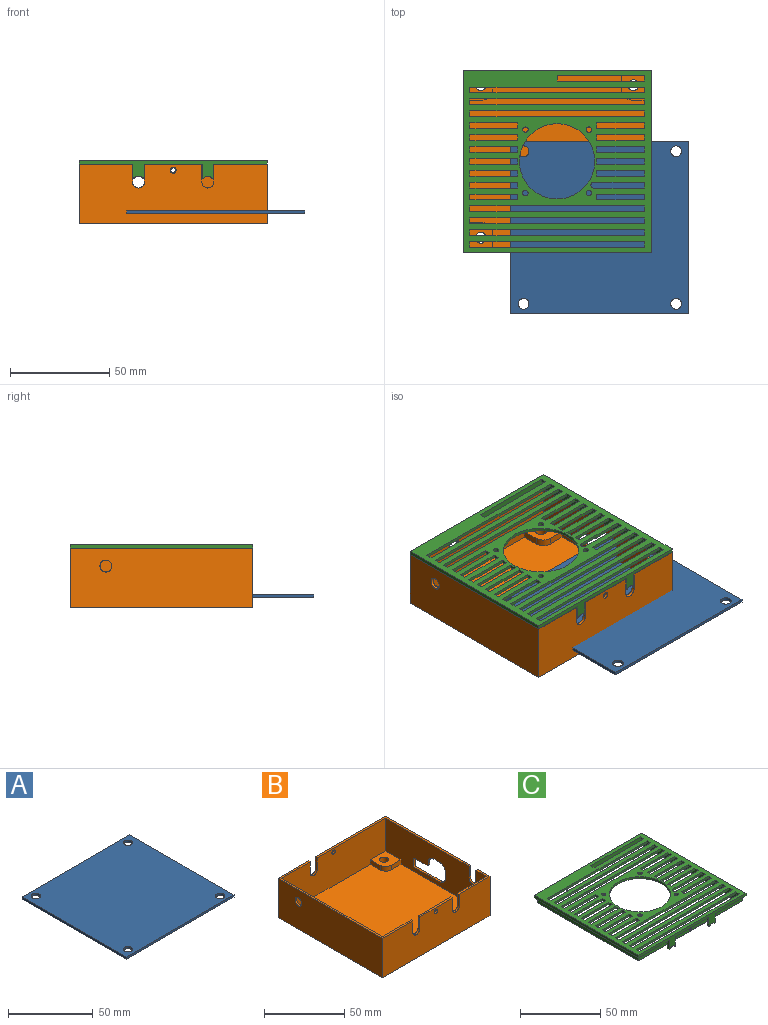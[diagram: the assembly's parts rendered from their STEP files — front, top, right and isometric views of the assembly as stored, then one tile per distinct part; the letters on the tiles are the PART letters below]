
ASSEMBLY  parts=3 mates=3
PART A: 10 faces, bbox 90x87x1.5 mm
  f0: plane 90x1.5mm, normal (0,1,0), area 135mm2, adj f1,f3,f4,f5
  f1: plane 87x1.5mm, normal (-1,0,0), area 130.5mm2, adj f0,f2,f4,f5
  f2: plane 90x1.5mm, normal (0,-1,0), area 135mm2, adj f1,f3,f4,f5
  f3: plane 87x1.5mm, normal (1,0,0), area 130.5mm2, adj f0,f2,f4,f5
  f4: plane 90x87mm, normal (0,0,1), area 7735mm2, adj f0,f1,f2,f3,f6,f7,f8,f9
  f5: plane 90x87mm, normal (0,0,-1), area 7735mm2, adj f0,f1,f2,f3,f6,f7,f8,f9
  f6: cylinder r=2.75mm len=5.5mm, axis (0,0,-1), area 25.9mm2, adj f4,f5
  f7: cylinder r=2.75mm len=5.5mm, axis (0,0,-1), area 25.9mm2, adj f4,f5
  f8: cylinder r=2.75mm len=5.5mm, axis (0,0,-1), area 25.9mm2, adj f4,f5
  f9: cylinder r=2.75mm len=5.5mm, axis (0,0,-1), area 25.9mm2, adj f4,f5
PART B: 61 faces, bbox 95x92x30 mm
  f0: plane 95x30mm, normal (0,-1,0), area 2706.7mm2, adj f2,f3,f5,f6,f12,f13,f49,f50
  f1: plane 75x62mm, normal (0,0,1), area 203.2mm2, adj f4,f5,f8,f11,f35,f52
  f2: plane 29x1.5mm, normal (0,0,1), area 43.5mm2, adj f0,f10,f49,f57
  f3: plane 27x11mm, normal (0,0,1), area 54.8mm2, adj f0,f4,f5,f10,f34,f51
  f4: plane 89x28.5mm, normal (-1,0,0), area 2074.2mm2, adj f1,f3,f7,f8,f10,f20,f22,f23
  f5: plane 92x30mm, normal (1,0,0), area 2392.2mm2, adj f0,f1,f3,f11,f13,f34,f35,f36
  f6: plane 92x27mm, normal (0,0,1), area 214.5mm2, adj f0,f8,f9,f10,f11,f12,f54,f55
  f7: plane 92x89mm, normal (0,0,1), area 7480.5mm2, adj f4,f8,f9,f10,f14,f15,f18,f19
  f8: plane 92x28.5mm, normal (0,-1,0), area 2452.3mm2, adj f1,f4,f6,f7,f9,f17,f19,f20
  f9: plane 89x28.5mm, normal (1,0,0), area 2413.7mm2, adj f6,f7,f8,f10,f15,f16,f17,f18
  f10: plane 92x28.5mm, normal (0,1,0), area 2384.2mm2, adj f2,f3,f4,f6,f7,f9,f14,f16
  f11: plane 95x30mm, normal (0,1,0), area 2774.8mm2, adj f1,f5,f6,f12,f13,f52,f53,f54
  f12: plane 92x30mm, normal (-1,0,0), area 2731.7mm2, adj f0,f6,f11,f13,f60
  f13: plane 95x92mm, normal (0,0,-1), area 8645mm2, adj f0,f5,f11,f12,f30,f31,f32,f33
  f14: plane 8.5x3.5mm, normal (1,0,0), area 29.8mm2, adj f7,f10,f16,f29
  f15: plane 8.5x3.5mm, normal (0,1,0), area 29.8mm2, adj f7,f9,f16,f29
  f16: plane 13.5x13.5mm, normal (0,0,1), area 153.1mm2, adj f9,f10,f14,f15,f29,f33
  f17: plane 13.5x13.5mm, normal (0,0,1), area 153.1mm2, adj f8,f9,f18,f19,f28,f32
  f18: plane 8.5x3.5mm, normal (0,-1,0), area 29.8mm2, adj f7,f9,f17,f28
  f19: plane 8.5x3.5mm, normal (1,0,0), area 29.8mm2, adj f7,f8,f17,f28
  f20: plane 13.5x13.5mm, normal (0,0,1), area 153.1mm2, adj f4,f8,f21,f22,f27,f31
  f21: plane 8.5x3.5mm, normal (-1,0,0), area 29.8mm2, adj f7,f8,f20,f27
  f22: plane 8.5x3.5mm, normal (0,-1,0), area 29.8mm2, adj f4,f7,f20,f27
  f23: plane 8.5x3.5mm, normal (0,1,0), area 29.8mm2, adj f4,f7,f25,f26
  f24: plane 8.5x3.5mm, normal (-1,0,0), area 29.8mm2, adj f7,f10,f25,f26
  f25: plane 13.5x13.5mm, normal (0,0,1), area 153.1mm2, adj f4,f10,f23,f24,f26,f30
  f26: cylinder r=5mm len=5mm, axis (0,0,1), area 27.5mm2, adj f7,f23,f24,f25
  f27: cylinder r=5mm len=5mm, axis (0,0,1), area 27.5mm2, adj f7,f20,f21,f22
  f28: cylinder r=5mm len=5mm, axis (0,0,1), area 27.5mm2, adj f7,f17,f18,f19
  f29: cylinder r=5mm len=5mm, axis (0,0,1), area 27.5mm2, adj f7,f14,f15,f16
  f30: cylinder r=2.75mm len=5.5mm, axis (0,0,-1), area 86.4mm2, adj f13,f25
  f31: cylinder r=2.75mm len=5.5mm, axis (0,0,-1), area 86.4mm2, adj f13,f20
  f32: cylinder r=2.75mm len=5.5mm, axis (0,0,-1), area 86.4mm2, adj f13,f17
  f33: cylinder r=2.75mm len=5.5mm, axis (0,0,-1), area 86.4mm2, adj f13,f16
  f34: plane 9x1.5mm, normal (0,1,0), area 13.5mm2, adj f3,f4,f5,f36
  f35: plane 9x1.5mm, normal (0,-1,0), area 13.5mm2, adj f1,f4,f5,f36
  f36: cylinder r=3mm len=6mm, axis (1,0,0), area 14.1mm2, adj f4,f5,f34,f35
  f37: plane 5x1.5mm, normal (0,0,-1), area 7.5mm2, adj f4,f5,f43,f45
  f38: plane 5x1.5mm, normal (0,1,0), area 7.5mm2, adj f4,f5,f43,f44
  f39: plane 22x1.5mm, normal (0,0,1), area 33mm2, adj f4,f5,f44,f46
  f40: plane 5x1.5mm, normal (0,-1,0), area 7.5mm2, adj f4,f5,f46,f47
  f41: plane 11x1.5mm, normal (0,0,-1), area 16.5mm2, adj f4,f5,f47,f48
  f42: plane 2x1.5mm, normal (0,-1,0), area 3mm2, adj f4,f5,f45,f48
  f43: cylinder r=5mm len=5mm, axis (1,0,0), area 11.8mm2, adj f4,f5,f37,f38
  f44: cylinder r=5mm len=5mm, axis (-1,0,0), area 11.8mm2, adj f4,f5,f38,f39
  f45: cylinder r=5mm len=5mm, axis (-1,0,0), area 11.8mm2, adj f4,f5,f37,f42
  f46: cylinder r=1mm len=1.5mm, axis (-1,0,0), area 2.4mm2, adj f4,f5,f39,f40
  f47: cylinder r=1mm len=1.5mm, axis (1,0,0), area 2.4mm2, adj f4,f5,f40,f41
  f48: cylinder r=1mm len=1.5mm, axis (1,0,0), area 2.4mm2, adj f4,f5,f41,f42
  f49: plane 9x1.5mm, normal (1,0,0), area 13.5mm2, adj f0,f2,f10,f50
  f50: cylinder r=3mm len=6mm, axis (0,-1,0), area 14.1mm2, adj f0,f10,f49,f51
  f51: plane 9x1.5mm, normal (-1,0,0), area 13.5mm2, adj f0,f3,f10,f50
  f52: plane 9x1.5mm, normal (-1,0,0), area 13.5mm2, adj f1,f8,f11,f53
  f53: cylinder r=3mm len=6mm, axis (0,-1,0), area 14.1mm2, adj f8,f11,f52,f54
  f54: plane 9x1.5mm, normal (1,0,0), area 13.5mm2, adj f6,f8,f11,f53
  f55: plane 9x1.5mm, normal (1,0,0), area 13.5mm2, adj f0,f6,f10,f56
  f56: cylinder r=3mm len=6mm, axis (0,-1,0), area 14.1mm2, adj f0,f10,f55,f57
  f57: plane 9x1.5mm, normal (-1,0,0), area 13.5mm2, adj f0,f2,f10,f56
  f58: cylinder r=1.5mm len=3mm, axis (0,-1,0), area 14.1mm2, adj f8,f11
  f59: cylinder r=1.5mm len=3mm, axis (0,-1,0), area 14.1mm2, adj f0,f10
  f60: cylinder r=3mm len=6mm, axis (-1,0,0), area 28.3mm2, adj f9,f12
PART C: 150 faces, bbox 95x92x9.1 mm
  f0: plane 90x6.5mm, normal (0,-1,0), area 533.5mm2, adj f2,f5,f27,f35,f36,f38,f94,f126
  f1: plane 88x1.5mm, normal (0,1,0), area 88mm2, adj f2,f5,f27,f94,f140,f141
  f2: plane 3x0.5mm, normal (1,0,0), area 1.5mm2, adj f0,f1,f27,f141
  f3: plane 27.2x11.2mm, normal (0,0,-1), area 55.4mm2, adj f4,f6,f30,f31,f122,f131
  f4: plane 9.7x3.7mm, normal (1,0,0), area 35.9mm2, adj f3,f6,f131,f148
  f5: plane 95x92mm, normal (0,0,1), area 4586.9mm2, adj f0,f1,f13,f14,f15,f16,f17,f18
  f6: plane 25.7x3.7mm, normal (0,-1,0), area 95.1mm2, adj f3,f4,f122,f149
  f7: plane 29.4x1.5mm, normal (0,0,-1), area 44.1mm2, adj f9,f30,f120,f123
  f8: plane 92x27.2mm, normal (0,0,-1), area 215.1mm2, adj f10,f28,f29,f30,f32,f34,f115,f118
  f9: plane 29.4x3.7mm, normal (0,-1,0), area 104.9mm2, adj f7,f120,f123,f125,f147
  f10: plane 25.7x3.7mm, normal (0,-1,0), area 95.1mm2, adj f8,f34,f118,f144
  f11: plane 75.2x62.2mm, normal (0,0,-1), area 203.8mm2, adj f12,f28,f31,f33,f116,f130
  f12: plane 60.7x3.7mm, normal (0,1,0), area 220.7mm2, adj f11,f33,f116,f126,f142
  f13: plane 24x1.5mm, normal (0,1,0), area 36mm2, adj f5,f27,f42,f107
  f14: plane 24x1.5mm, normal (0,-1,0), area 36mm2, adj f5,f27,f42,f107
  f15: plane 25.5x1.5mm, normal (0,1,0), area 38.2mm2, adj f5,f27,f46,f127
  f16: plane 25.5x1.5mm, normal (0,-1,0), area 38.2mm2, adj f5,f27,f46,f127
  f17: plane 24x1.5mm, normal (0,1,0), area 36mm2, adj f5,f27,f50,f104
  f18: plane 24x1.5mm, normal (0,-1,0), area 36mm2, adj f5,f27,f50,f104
  f19: plane 24x1.5mm, normal (0,-1,0), area 36mm2, adj f5,f27,f69,f101
  f20: plane 24x1.5mm, normal (0,1,0), area 36mm2, adj f5,f27,f69,f101
  f21: plane 24x1.5mm, normal (0,-1,0), area 36mm2, adj f5,f27,f73,f99
  f22: plane 24x1.5mm, normal (0,1,0), area 36mm2, adj f5,f27,f73,f99
  f23: plane 24x1.5mm, normal (0,-1,0), area 36mm2, adj f5,f27,f77,f97
  f24: plane 24x1.5mm, normal (0,1,0), area 36mm2, adj f5,f27,f77,f97
  f25: plane 24x1.5mm, normal (0,-1,0), area 36mm2, adj f5,f27,f81,f95
  f26: plane 24x1.5mm, normal (0,1,0), area 36mm2, adj f5,f27,f81,f95
  f27: plane 90x87mm, normal (0,0,-1), area 3544.9mm2, adj f0,f1,f2,f13,f14,f15,f16,f17
  f28: plane 95x9.08mm, normal (0,1,0), area 226.2mm2, adj f5,f8,f11,f29,f31,f113,f115,f116
  f29: plane 92x2mm, normal (-1,0,0), area 184mm2, adj f5,f8,f28,f30
  f30: plane 95x9.08mm, normal (0,-1,0), area 262.5mm2, adj f3,f5,f7,f8,f29,f31,f118,f119
  f31: plane 92x9.08mm, normal (1,0,0), area 220.2mm2, adj f3,f5,f11,f28,f30,f128,f130,f131
  f32: plane 25.7x3.7mm, normal (0,1,0), area 95.1mm2, adj f8,f34,f115,f146
  f33: plane 73.7x3.7mm, normal (1,0,0), area 272.7mm2, adj f11,f12,f130,f143
  f34: plane 89x3.7mm, normal (-1,0,0), area 329.3mm2, adj f8,f10,f32,f145
  f35: plane 91.2x89mm, normal (0,0,-1), area 88.9mm2, adj f0,f36,f37,f38,f114,f115,f116,f117
  f36: plane 87x5mm, normal (-1,0,0), area 435mm2, adj f0,f27,f35,f37
  f37: plane 90x6.5mm, normal (0,1,0), area 577.5mm2, adj f5,f27,f35,f36,f38,f63,f65,f125
  f38: plane 87x5mm, normal (1,0,0), area 435mm2, adj f0,f27,f35,f37
  f39: plane 24x1.5mm, normal (0,1,0), area 36mm2, adj f5,f27,f40,f106
  f40: plane 3x1.5mm, normal (1,0,0), area 4.5mm2, adj f5,f27,f39,f41
  f41: plane 24x1.5mm, normal (0,-1,0), area 36mm2, adj f5,f27,f40,f106
  f42: plane 3x1.5mm, normal (-1,0,0), area 4.5mm2, adj f5,f13,f14,f27
  f43: plane 24x1.5mm, normal (0,1,0), area 36mm2, adj f5,f27,f44,f105
  f44: plane 3x1.5mm, normal (1,0,0), area 4.5mm2, adj f5,f27,f43,f45
  f45: plane 24x1.5mm, normal (0,-1,0), area 36mm2, adj f5,f27,f44,f105
  f46: plane 3x1.5mm, normal (-1,0,0), area 4.5mm2, adj f5,f15,f16,f27
  f47: plane 24x1.5mm, normal (0,1,0), area 36mm2, adj f5,f27,f48,f103
  f48: plane 3x1.5mm, normal (1,0,0), area 4.5mm2, adj f5,f27,f47,f49
  f49: plane 24x1.5mm, normal (0,-1,0), area 36mm2, adj f5,f27,f48,f103
  f50: plane 3x1.5mm, normal (-1,0,0), area 4.5mm2, adj f5,f17,f18,f27
  f51: plane 88x1.5mm, normal (0,1,0), area 132mm2, adj f5,f27,f52,f54
  f52: plane 3x1.5mm, normal (1,0,0), area 4.5mm2, adj f5,f27,f51,f53
  f53: plane 88x1.5mm, normal (0,-1,0), area 132mm2, adj f5,f27,f52,f54
  f54: plane 3x1.5mm, normal (-1,0,0), area 4.5mm2, adj f5,f27,f51,f53
  f55: plane 88x1.5mm, normal (0,1,0), area 132mm2, adj f5,f27,f56,f58
  f56: plane 3x1.5mm, normal (1,0,0), area 4.5mm2, adj f5,f27,f55,f57
  f57: plane 88x1.5mm, normal (0,-1,0), area 132mm2, adj f5,f27,f56,f58
  f58: plane 3x1.5mm, normal (-1,0,0), area 4.5mm2, adj f5,f27,f55,f57
  f59: plane 88x1.5mm, normal (0,1,0), area 132mm2, adj f5,f27,f60,f62
  f60: plane 3x1.5mm, normal (1,0,0), area 4.5mm2, adj f5,f27,f59,f61
  f61: plane 88x1.5mm, normal (0,-1,0), area 132mm2, adj f5,f27,f60,f62
  f62: plane 3x1.5mm, normal (-1,0,0), area 4.5mm2, adj f5,f27,f59,f61
  f63: plane 3x1.5mm, normal (1,0,0), area 4.5mm2, adj f5,f27,f37,f64
  f64: plane 88x1.5mm, normal (0,-1,0), area 132mm2, adj f5,f27,f63,f65
  f65: plane 3x1.5mm, normal (-1,0,0), area 4.5mm2, adj f5,f27,f37,f64
  f66: plane 24x1.5mm, normal (0,-1,0), area 36mm2, adj f5,f27,f67,f102
  f67: plane 3x1.5mm, normal (1,0,0), area 4.5mm2, adj f5,f27,f66,f68
  f68: plane 24x1.5mm, normal (0,1,0), area 36mm2, adj f5,f27,f67,f102
  f69: plane 3x1.5mm, normal (-1,0,0), area 4.5mm2, adj f5,f19,f20,f27
  f70: plane 24x1.5mm, normal (0,-1,0), area 36mm2, adj f5,f27,f71,f100
  f71: plane 3x1.5mm, normal (1,0,0), area 4.5mm2, adj f5,f27,f70,f72
  f72: plane 24x1.5mm, normal (0,1,0), area 36mm2, adj f5,f27,f71,f100
  f73: plane 3x1.5mm, normal (-1,0,0), area 4.5mm2, adj f5,f21,f22,f27
  f74: plane 24x1.5mm, normal (0,-1,0), area 36mm2, adj f5,f27,f75,f98
  f75: plane 3x1.5mm, normal (1,0,0), area 4.5mm2, adj f5,f27,f74,f76
  f76: plane 24x1.5mm, normal (0,1,0), area 36mm2, adj f5,f27,f75,f98
  f77: plane 3x1.5mm, normal (-1,0,0), area 4.5mm2, adj f5,f23,f24,f27
  f78: plane 24x1.5mm, normal (0,-1,0), area 36mm2, adj f5,f27,f79,f96
  f79: plane 3x1.5mm, normal (1,0,0), area 4.5mm2, adj f5,f27,f78,f80
  f80: plane 24x1.5mm, normal (0,1,0), area 36mm2, adj f5,f27,f79,f96
  f81: plane 3x1.5mm, normal (-1,0,0), area 4.5mm2, adj f5,f25,f26,f27
  f82: plane 88x1.5mm, normal (0,-1,0), area 132mm2, adj f5,f27,f83,f85
  f83: plane 3x1.5mm, normal (1,0,0), area 4.5mm2, adj f5,f27,f82,f84
  f84: plane 88x1.5mm, normal (0,1,0), area 132mm2, adj f5,f27,f83,f85
  f85: plane 3x1.5mm, normal (-1,0,0), area 4.5mm2, adj f5,f27,f82,f84
  f86: plane 88x1.5mm, normal (0,-1,0), area 132mm2, adj f5,f27,f87,f89
  f87: plane 3x1.5mm, normal (1,0,0), area 4.5mm2, adj f5,f27,f86,f88
  f88: plane 88x1.5mm, normal (0,1,0), area 132mm2, adj f5,f27,f87,f89
  f89: plane 3x1.5mm, normal (-1,0,0), area 4.5mm2, adj f5,f27,f86,f88
  f90: plane 88x1.5mm, normal (0,-1,0), area 132mm2, adj f5,f27,f91,f93
  f91: plane 3x1.5mm, normal (1,0,0), area 4.5mm2, adj f5,f27,f90,f92
  f92: plane 88x1.5mm, normal (0,1,0), area 132mm2, adj f5,f27,f91,f93
  f93: plane 3x1.5mm, normal (-1,0,0), area 4.5mm2, adj f5,f27,f90,f92
  f94: plane 3x1.5mm, normal (-1,0,0), area 4.5mm2, adj f0,f1,f5,f27
  f95: plane 3x1.5mm, normal (1,0,0), area 4.5mm2, adj f5,f25,f26,f27
  f96: plane 3x1.5mm, normal (-1,0,0), area 4.5mm2, adj f5,f27,f78,f80
  f97: plane 3x1.5mm, normal (1,0,0), area 4.5mm2, adj f5,f23,f24,f27
  f98: plane 3x1.5mm, normal (-1,0,0), area 4.5mm2, adj f5,f27,f74,f76
  f99: plane 3x1.5mm, normal (1,0,0), area 4.5mm2, adj f5,f21,f22,f27
  f100: plane 3x1.5mm, normal (-1,0,0), area 4.5mm2, adj f5,f27,f70,f72
  f101: plane 3x1.5mm, normal (1,0,0), area 4.5mm2, adj f5,f19,f20,f27
  f102: plane 3x1.5mm, normal (-1,0,0), area 4.5mm2, adj f5,f27,f66,f68
  f103: plane 3x1.5mm, normal (-1,0,0), area 4.5mm2, adj f5,f27,f47,f49
  f104: plane 3x1.5mm, normal (1,0,0), area 4.5mm2, adj f5,f17,f18,f27
  f105: plane 3x1.5mm, normal (-1,0,0), area 4.5mm2, adj f5,f27,f43,f45
  f106: plane 3x1.5mm, normal (-1,0,0), area 4.5mm2, adj f5,f27,f39,f41
  f107: plane 3x1.5mm, normal (1,0,0), area 4.5mm2, adj f5,f13,f14,f27
  f108: cylinder r=19mm len=38mm, axis (0,0,1), area 179.1mm2, adj f5,f27
  f109: cylinder r=1.35mm len=2.7mm, axis (0,0,1), area 12.7mm2, adj f5,f27
  f110: cylinder r=1.35mm len=2.7mm, axis (0,0,1), area 12.7mm2, adj f5,f27
  f111: cylinder r=1.35mm len=2.7mm, axis (0,0,1), area 12.7mm2, adj f5,f27
  f112: cylinder r=1.35mm len=2.7mm, axis (0,0,1), area 12.7mm2, adj f5,f27
  f113: cylinder r=2.8mm len=4.2mm, axis (0,-1,0), area 7.1mm2, adj f28,f114,f138,f139
  f114: plane 5.6x2.58mm, normal (0,-1,0), area 11mm2, adj f35,f113,f115,f116,f138,f139
  f115: plane 6.68x2.3mm, normal (-1,0,0), area 10.3mm2, adj f8,f28,f32,f35,f114,f139,f146
  f116: plane 6.68x2.3mm, normal (1,0,0), area 10.3mm2, adj f11,f12,f28,f35,f114,f138,f142
  f117: plane 5.6x2.58mm, normal (0,1,0), area 11mm2, adj f35,f118,f119,f120,f136,f137
  f118: plane 6.68x2.3mm, normal (-1,0,0), area 10.3mm2, adj f8,f10,f30,f35,f117,f136,f144
  f119: cylinder r=2.8mm len=4.2mm, axis (0,1,0), area 7.1mm2, adj f30,f117,f136,f137
  f120: plane 6.68x2.3mm, normal (1,0,0), area 10.3mm2, adj f7,f9,f30,f35,f117,f137,f147
  f121: plane 5.6x2.58mm, normal (0,1,0), area 11mm2, adj f35,f122,f123,f124,f134,f135
  f122: plane 6.68x2.3mm, normal (1,0,0), area 10.3mm2, adj f3,f6,f30,f35,f121,f135,f149
  f123: plane 6.68x2.3mm, normal (-1,0,0), area 10.3mm2, adj f7,f9,f30,f35,f121,f134,f147
  f124: cylinder r=2.8mm len=4.2mm, axis (0,1,0), area 7.1mm2, adj f30,f121,f134,f135
  f125: cylinder r=1.2mm len=2.4mm, axis (0,1,0), area 6.8mm2, adj f9,f37,f147
  f126: cylinder r=1.2mm len=2.4mm, axis (0,1,0), area 6.8mm2, adj f0,f12,f142
  f127: cylinder r=1.5mm len=3mm, axis (0,0,1), area 7.1mm2, adj f5,f15,f16,f27
  f128: cylinder r=2.8mm len=4.2mm, axis (-1,0,0), area 7.1mm2, adj f31,f129,f132,f133
  f129: plane 5.6x2.58mm, normal (-1,0,0), area 11mm2, adj f35,f128,f130,f131,f132,f133
  f130: plane 6.68x2.3mm, normal (0,1,0), area 10.3mm2, adj f11,f31,f33,f35,f129,f133,f143
  f131: plane 6.68x2.3mm, normal (0,-1,0), area 10.3mm2, adj f3,f4,f31,f35,f129,f132,f148
  f132: cylinder r=0.4mm len=1.5mm, axis (-1,0,0), area 1.5mm2, adj f31,f128,f129,f131
  f133: cylinder r=0.4mm len=1.5mm, axis (-1,0,0), area 1.5mm2, adj f31,f128,f129,f130
  f134: cylinder r=0.4mm len=1.5mm, axis (0,1,0), area 1.5mm2, adj f30,f121,f123,f124
  f135: cylinder r=0.4mm len=1.5mm, axis (0,1,0), area 1.5mm2, adj f30,f121,f122,f124
  f136: cylinder r=0.4mm len=1.5mm, axis (0,1,0), area 1.5mm2, adj f30,f117,f118,f119
  f137: cylinder r=0.4mm len=1.5mm, axis (0,1,0), area 1.5mm2, adj f30,f117,f119,f120
  f138: cylinder r=0.4mm len=1.5mm, axis (0,-1,0), area 1.5mm2, adj f28,f113,f114,f116
  f139: cylinder r=0.4mm len=1.5mm, axis (0,-1,0), area 1.5mm2, adj f28,f113,f114,f115
  f140: plane 3x1mm, normal (1,0,0), area 3mm2, adj f0,f1,f5,f141
  f141: plane 44x3mm, normal (0,0,-1), area 132mm2, adj f0,f1,f2,f140
  f142: plane 60.7x0.8mm, normal (0,0.71,-0.71), area 67.3mm2, adj f12,f35,f116,f126,f143
  f143: plane 73.7x0.8mm, normal (0.71,0,-0.71), area 82.9mm2, adj f33,f35,f130,f142
  f144: plane 25.7x0.8mm, normal (0,-0.71,-0.71), area 28.6mm2, adj f10,f35,f118,f145
  f145: plane 89x0.8mm, normal (-0.71,0,-0.71), area 99.8mm2, adj f34,f35,f144,f146
  f146: plane 25.7x0.8mm, normal (0,0.71,-0.71), area 28.6mm2, adj f32,f35,f115,f145
  f147: plane 29.4x0.8mm, normal (0,-0.71,-0.71), area 32.3mm2, adj f9,f35,f120,f123,f125
  f148: plane 9.7x0.8mm, normal (0.71,0,-0.71), area 10.5mm2, adj f4,f35,f131,f149
  f149: plane 25.7x0.8mm, normal (0,-0.71,-0.71), area 28.6mm2, adj f6,f35,f122,f148
PLACE A t=(34.72,-26.18,0.06)mm
PLACE B t=(13.19,7.2,-4.94)mm
PLACE C t=(13.19,7.2,27.06)mm
MATE planar B.f5 <-> C.f31  axis (1,0,0) through (60.69,15.7,25.06)mm
MATE planar B.f32 <-> A.f6  axis (0,0,1) through (-25.31,45.7,0.06)mm
MATE planar C.f3 <-> B.f3  axis (0,0,1) through (60.69,-38.8,25.06)mm
